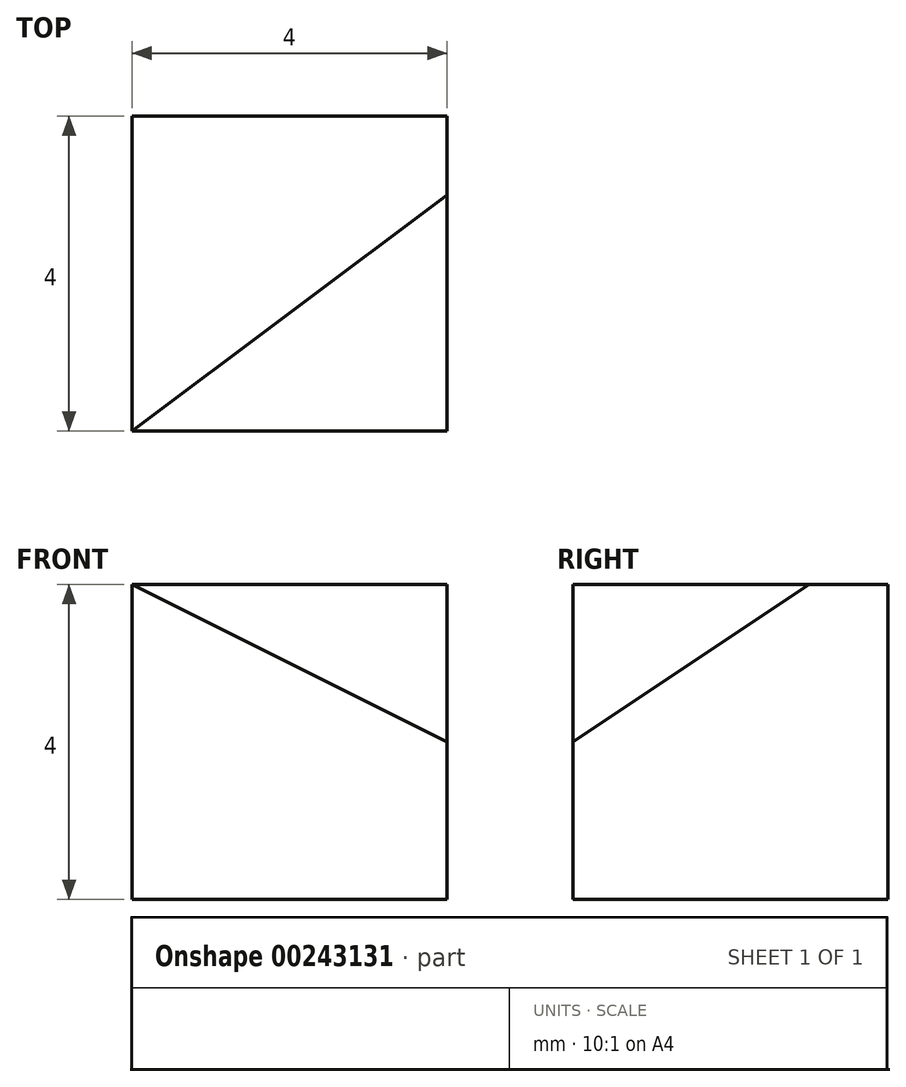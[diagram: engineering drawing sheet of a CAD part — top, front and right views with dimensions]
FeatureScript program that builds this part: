
annotation { "Feature Type Name" : "Feature", "Feature Type Description" : "" }
export const myFeature = defineFeature(function(context is Context, id is Id, definition is map)
    precondition{}
    {
        {
            var Q0;
            Q0=qCreatedBy(makeId("Front.planeOp"),FACE);
            var sketch = newSketch(context, id + "F0", { "sketchPlane" : qUnion([Q0])});
            skLineSegment(sketch, "E0.bottom", {"start": v(0, 0) * mm, "end": v(4, 0) * mm});
            skLineSegment(sketch, "E0.top", {"start": v(0, 4) * mm, "end": v(4, 4) * mm});
            skLineSegment(sketch, "E0.left", {"start": v(0, 0) * mm, "end": v(0, 4) * mm});
            skLineSegment(sketch, "E0.right", {"start": v(4, 0) * mm, "end": v(4, 4) * mm});
            skSolve(sketch);
        }
        {
            var Q0;
            Q0 = qSketchRegion(id + "F0", true);
            extrude(context, id + "F1", {"entities" : qUnion([Q0]), "depth" : 4 * mm});
        }
        {
            var Q0;
            Q0=makeQuery(id+"F1.opExtrude","CAP_FACE",FACE,{"disambiguationData":[OSD([sQuery(id+"F0.wireOp",EDGE,"E0.bottom"),sQuery(id+"F0.wireOp",EDGE,"E0.top"),sQuery(id+"F0.wireOp",EDGE,"E0.left"),sQuery(id+"F0.wireOp",EDGE,"E0.right")])],"isStart":false});
            var sketch = newSketch(context, id + "F2", { "sketchPlane" : qUnion([Q0])});
            skPoint(sketch, "E1", {"position": v(4, 2) * mm});
            skSolve(sketch);
        }
        {
            var Q0;
            Q0=makeQuery(id+"F1.opExtrude","SWEPT_FACE",FACE,{"disambiguationData":[OSD([sQuery(id+"F0.wireOp",EDGE,"E0.right")])]});
            var sketch = newSketch(context, id + "F3", { "sketchPlane" : qUnion([Q0])});
            skPoint(sketch, "E2", {"position": v(-1, 4) * mm});
            skSolve(sketch);
        }
        {
            var Q0;
            Q0=makeQuery(id+"F1.opExtrude","CAP_EDGE",EDGE,{"disambiguationData":[OSD([sQuery(id+"F0.wireOp",EDGE,"E0.right")])],"isStart":false});
            cPoint(context, id + "F4", {"entities" : qUnion([Q0]), "parameter" : 0.5});
        }
        {
            var Q0;
            Q0=sQuery(id+"F3.wireOp",VERTEX,"E2");
            var Q1;
            Q1 = qCreatedBy(id + "F4" ,VERTEX);
            var Q2;
            Q2=makeQuery(id+"F1.opExtrude","CAP_VERTEX",VERTEX,{"disambiguationData":[OSD([sQuery(id+"F0.wireOp",EDGE,"E0.top"),sQuery(id+"F0.wireOp",EDGE,"E0.left")])],"isStart":false});
            cPlane(context, id + "F5", {"entities" : qUnion([Q0, Q1, Q2]), "cplaneType" : CPlaneType.THREE_POINT, "offset" : 25 * mm, "width" : 150 * mm, "height" : 150 * mm});
        }
        {
            var Q0;
            Q0=qCreatedBy(id+"F5.planeOp",FACE);
            var sketch = newSketch(context, id + "F6", { "sketchPlane" : qUnion([Q0])});
            skPoint(sketch, "E3.0", {"position": v(2.2, 1.39) * mm});
            skPoint(sketch, "E3.1", {"position": v(-2.13, -1.1) * mm});
            skPoint(sketch, "E3.2", {"position": v(2.2, -2.22) * mm});
            skLineSegment(sketch, "E4", {"start": v(-2.13, -1.1) * mm, "end": v(2.2, 1.39) * mm});
            skLineSegment(sketch, "E5", {"start": v(2.2, -2.22) * mm, "end": v(-2.13, -1.1) * mm});
            skLineSegment(sketch, "E6", {"start": v(2.2, -2.22) * mm, "end": v(2.2, 1.39) * mm});
            skSolve(sketch);
        }
        {
            var Q0;
            Q0 = qSketchRegion(id + "F6", true);
            extrude(context, id + "F7", {"entities" : qUnion([Q0]), "operationType" : NewBodyOperationType.REMOVE, "depth" : 25 * mm});
        }
    });
